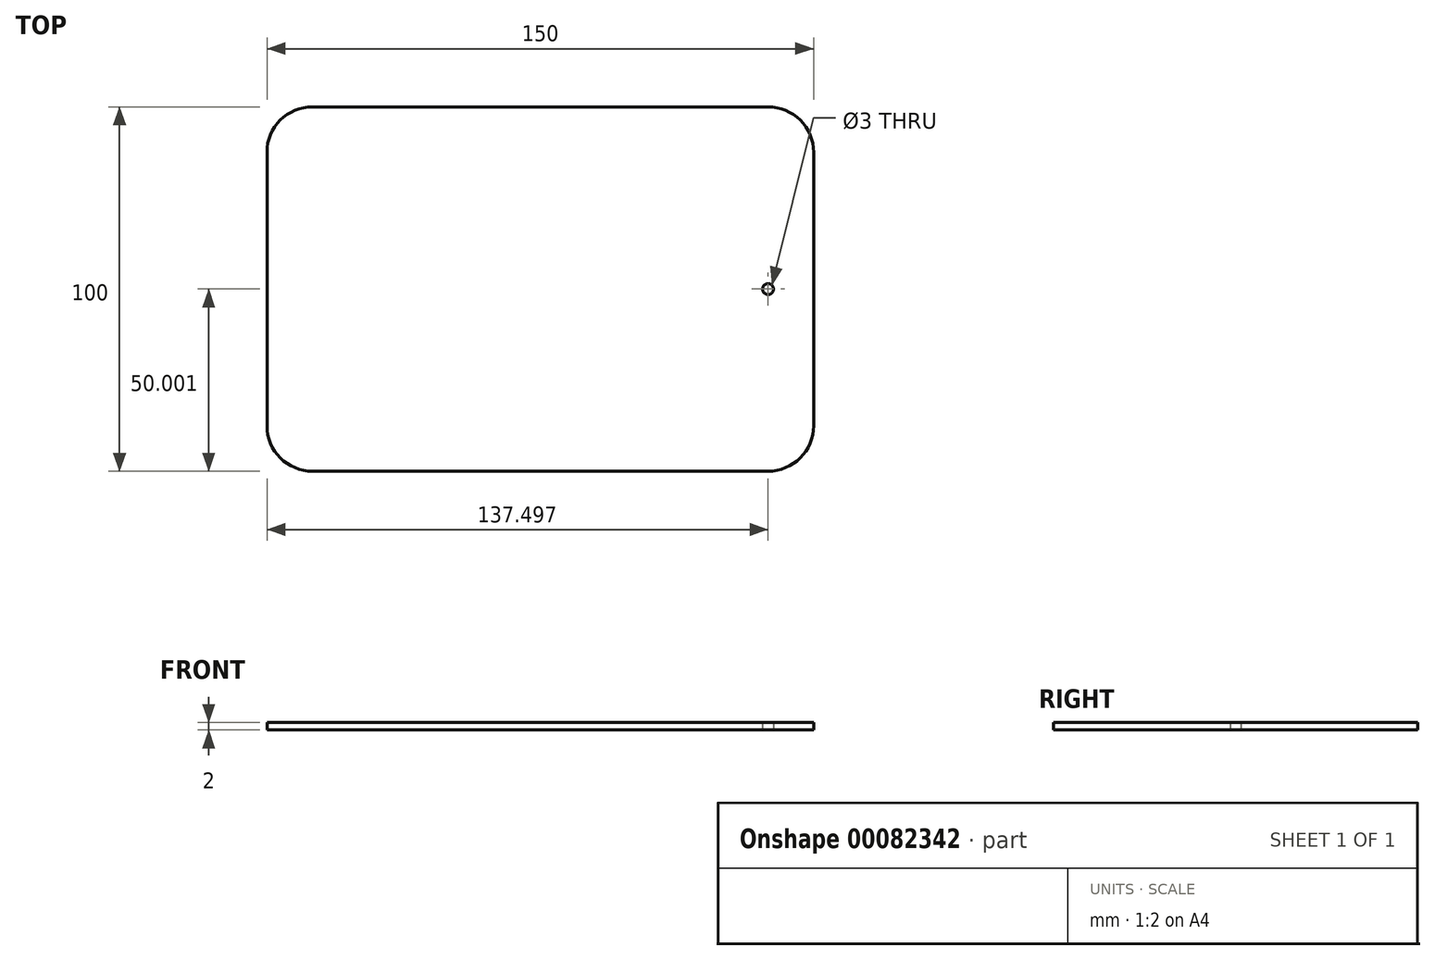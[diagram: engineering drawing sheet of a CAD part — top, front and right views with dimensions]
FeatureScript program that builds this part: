
annotation { "Feature Type Name" : "Feature", "Feature Type Description" : "" }
export const myFeature = defineFeature(function(context is Context, id is Id, definition is map)
    precondition{}
    {
        {
            var Q0;
            Q0=qCreatedBy(makeId("Top.planeOp"),FACE);
            var sketch = newSketch(context, id + "F0", { "sketchPlane" : qUnion([Q0])});
            skLineSegment(sketch, "E0.bottom", {"start": v(-60.03, 59.97) * mm, "end": v(89.97, 59.97) * mm});
            skLineSegment(sketch, "E0.top", {"start": v(-60.03, -40.03) * mm, "end": v(89.97, -40.03) * mm});
            skLineSegment(sketch, "E0.left", {"start": v(-60.03, 59.97) * mm, "end": v(-60.03, -40.03) * mm});
            skLineSegment(sketch, "E0.right", {"start": v(89.97, 59.97) * mm, "end": v(89.97, -40.03) * mm});
            skPoint(sketch, "E0.middle", {"position": v(14.97, 9.97) * mm});
            skCircle(sketch, "E1", {"center": v(77.47, 9.97) * mm, "radius": 1.5 * mm});
            skSolve(sketch);
        }
        {
            var Q0;
            Q0=makeQuery(id+"F0.imprint","IMPRINT",FACE,{"disambiguationData":[TD([[makeQuery(id+"F0.imprint","IMPRINT",EDGE,{"derivedFrom":sQuery(id+"F0.wireOp",EDGE,"E0.bottom")}),-1.0]])]});
            extrude(context, id + "F1", {"entities" : qUnion([Q0]), "depth" : 2 * mm});
        }
        {
            var Q0;
            Q0=makeQuery(id+"F1.opExtrude","SWEPT_EDGE",EDGE,{"disambiguationData":[OSD([sQuery(id+"F0.wireOp",EDGE,"E0.bottom"),sQuery(id+"F0.wireOp",EDGE,"E0.left")])]});
            var Q1;
            Q1=makeQuery(id+"F1.opExtrude","SWEPT_EDGE",EDGE,{"disambiguationData":[OSD([sQuery(id+"F0.wireOp",EDGE,"E0.top"),sQuery(id+"F0.wireOp",EDGE,"E0.left")])]});
            var Q2;
            Q2=makeQuery(id+"F1.opExtrude","SWEPT_EDGE",EDGE,{"disambiguationData":[OSD([sQuery(id+"F0.wireOp",EDGE,"E0.top"),sQuery(id+"F0.wireOp",EDGE,"E0.right")])]});
            var Q3;
            Q3=makeQuery(id+"F1.opExtrude","SWEPT_EDGE",EDGE,{"disambiguationData":[OSD([sQuery(id+"F0.wireOp",EDGE,"E0.bottom"),sQuery(id+"F0.wireOp",EDGE,"E0.right")])]});
            fillet(context, id + "F2", {"entities" : qUnion([Q0, Q1, Q2, Q3]), "radius" : 12.5 * mm, "tangentPropagation" : true, "allowEdgeOverflow" : false});
        }
    });
